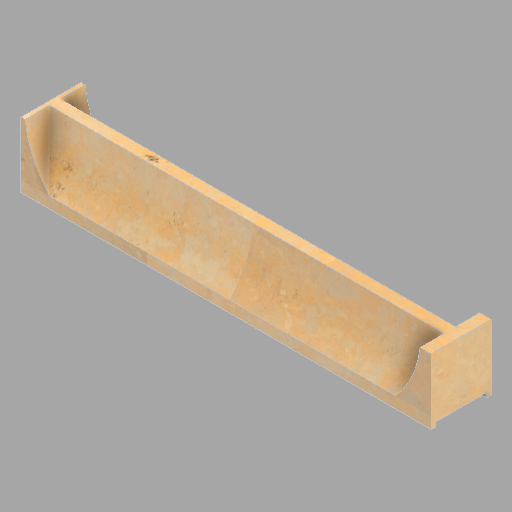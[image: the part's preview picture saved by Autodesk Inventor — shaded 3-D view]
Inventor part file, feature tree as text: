
AUTODESK INVENTOR PART (.ipt)
format: ipt  version: 2022.2 (Build 262287010, 287A)  size: 280,064 bytes
history: native  units: in
note: dims shown in document units (in); Inventor stores cm internally (conversion verified against a paired STEP export)
features: other x1, plane x1, extrude x1, sketch x1
ambient origin geometry x8: Origin, YZ Plane, XZ Plane, XY Plane, X Axis, Y Axis, Z Axis, Center Point
bodies: Solid1 (feature_tree)
feature tree (4):
  other  "North (6) (1)"
  plane  "Work Plane1"
  extrude  "Extrusion1"  Depth=1.0in
  sketch  "Sketch1"  dims[d2=-18.3125in d3=1.0in d4=1.0in d5=8.75in d6=8.75in d7=0.375in d8=0.375in d9=0.375in d10=1.0in d11=5.75in d12=18.1875in d13=16.9375in d14=0.0in d15=0.0in]
